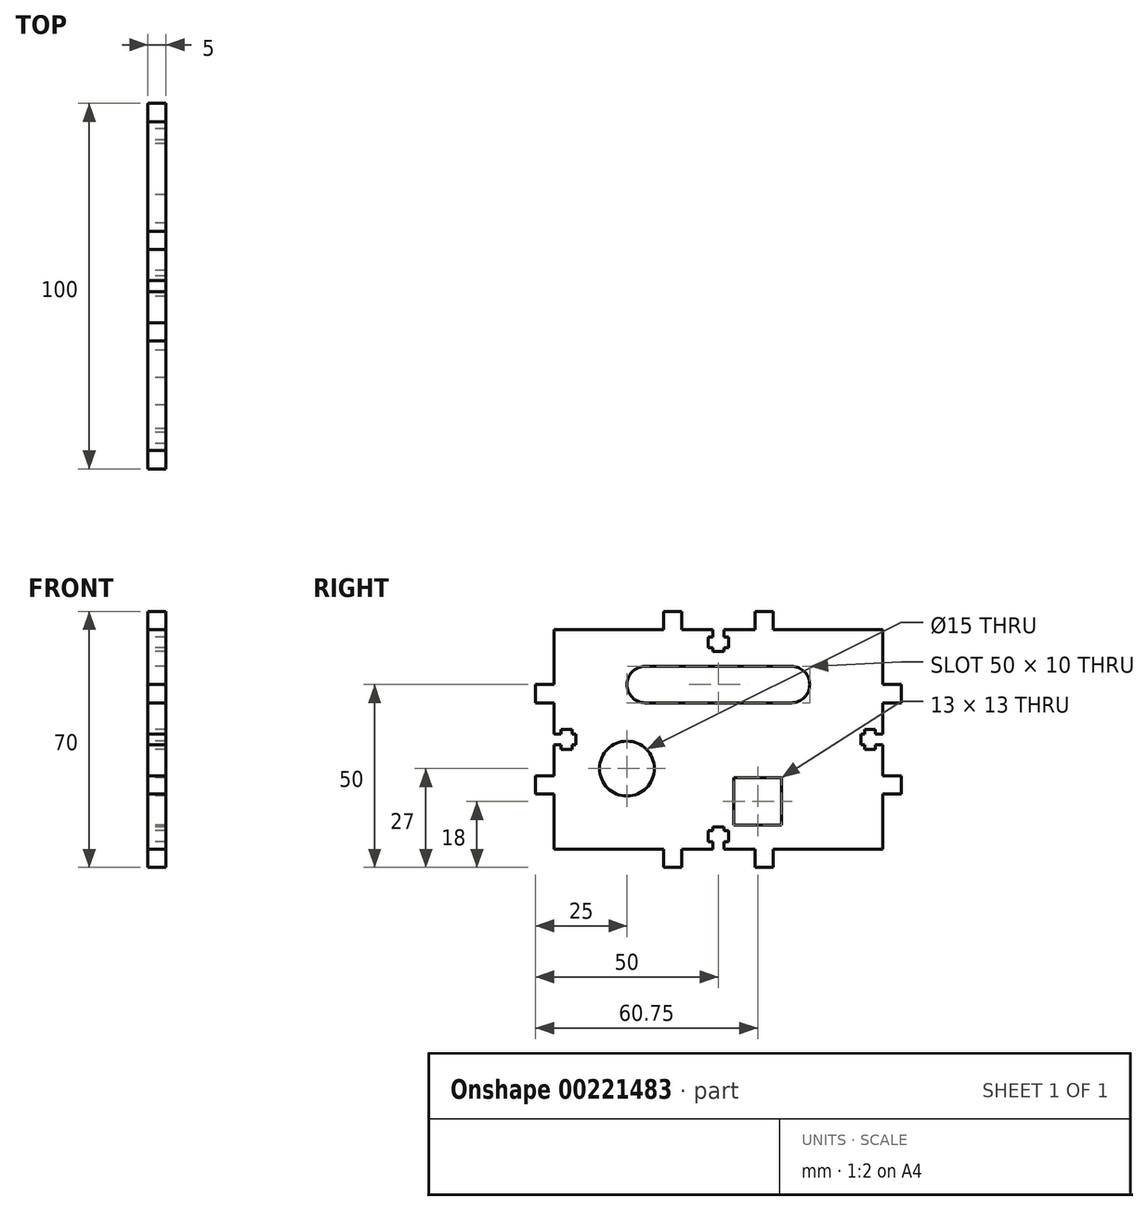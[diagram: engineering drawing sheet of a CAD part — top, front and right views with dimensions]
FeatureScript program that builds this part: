
annotation { "Feature Type Name" : "Feature", "Feature Type Description" : "" }
export const myFeature = defineFeature(function(context is Context, id is Id, definition is map)
    precondition{}
    {
        {
            assignVariable(context, id + "F0", {"name" : "thickness", "anyValue" : 5 * mm});
        }
        {
            var Q0;
            Q0=qCreatedBy(makeId("Right.planeOp"),FACE);
            var sketch = newSketch(context, id + "F1", { "sketchPlane" : qUnion([Q0])});
            skLineSegment(sketch, "E0.bottom", {"start": v(0, 0) * mm, "end": v(30, 0) * mm});
            skLineSegment(sketch, "E0.top", {"start": v(0, 60) * mm, "end": v(30, 60) * mm});
            skLineSegment(sketch, "E0.left", {"start": v(0, 0) * mm, "end": v(0, 15) * mm});
            skLineSegment(sketch, "E0.right", {"start": v(90, 0) * mm, "end": v(90, 15) * mm});
            skLineSegment(sketch, "E1", {"start": v(0, 45) * mm, "end": v(-5, 45) * mm});
            skLineSegment(sketch, "E2", {"start": v(-5, 45) * mm, "end": v(-5, 40) * mm});
            skLineSegment(sketch, "E3", {"start": v(-5, 40) * mm, "end": v(0, 40) * mm});
            skLineSegment(sketch, "E4", {"start": v(0, 20) * mm, "end": v(-5, 20) * mm});
            skLineSegment(sketch, "E5", {"start": v(-5, 20) * mm, "end": v(-5, 15) * mm});
            skLineSegment(sketch, "E6", {"start": v(-5, 15) * mm, "end": v(0, 15) * mm});
            skLineSegment(sketch, "E7", {"start": v(45, 60) * mm, "end": v(45, 0) * mm, "construction": true});
            skLineSegment(sketch, "E8", {"start": v(90, 30) * mm, "end": v(0, 30) * mm, "construction": true});
            skLineSegment(sketch, "E9", {"start": v(0, 31.5) * mm, "end": v(2, 31.5) * mm});
            skLineSegment(sketch, "E10", {"start": v(2, 31.5) * mm, "end": v(2, 32.75) * mm});
            skLineSegment(sketch, "E11", {"start": v(2, 32.75) * mm, "end": v(5, 32.75) * mm});
            skLineSegment(sketch, "E12", {"start": v(5, 32.75) * mm, "end": v(5, 31.5) * mm});
            skLineSegment(sketch, "E13", {"start": v(5, 27.25) * mm, "end": v(2, 27.25) * mm});
            skLineSegment(sketch, "E14", {"start": v(2, 27.25) * mm, "end": v(2, 28.5) * mm});
            skLineSegment(sketch, "E15", {"start": v(2, 28.5) * mm, "end": v(0, 28.5) * mm});
            skLineSegment(sketch, "E16", {"start": v(5, 31.5) * mm, "end": v(6, 31.5) * mm});
            skLineSegment(sketch, "E17", {"start": v(6, 31.5) * mm, "end": v(6, 28.5) * mm});
            skLineSegment(sketch, "E18", {"start": v(6, 28.5) * mm, "end": v(5, 28.5) * mm});
            skLineSegment(sketch, "E19.trimOffspring", {"start": v(5, 28.5) * mm, "end": v(5, 27.25) * mm});
            skPoint(sketch, "E20", {"position": v(6, 30) * mm});
            skLineSegment(sketch, "E21.MirrorCS", {"start": v(85, 31.5) * mm, "end": v(84, 31.5) * mm});
            skLineSegment(sketch, "E22.MirrorCS", {"start": v(88, 31.5) * mm, "end": v(88, 32.75) * mm});
            skLineSegment(sketch, "E23.MirrorCS", {"start": v(84, 28.5) * mm, "end": v(85, 28.5) * mm});
            skLineSegment(sketch, "E24.MirrorCS", {"start": v(88, 27.25) * mm, "end": v(88, 28.5) * mm});
            skLineSegment(sketch, "E25.MirrorCS", {"start": v(85, 32.75) * mm, "end": v(85, 31.5) * mm});
            skLineSegment(sketch, "E26.MirrorCS", {"start": v(85, 28.5) * mm, "end": v(85, 27.25) * mm});
            skLineSegment(sketch, "E27.MirrorCS", {"start": v(88, 28.5) * mm, "end": v(90, 28.5) * mm});
            skLineSegment(sketch, "E28.MirrorCS", {"start": v(84, 31.5) * mm, "end": v(84, 28.5) * mm});
            skLineSegment(sketch, "E29.MirrorCS", {"start": v(90, 31.5) * mm, "end": v(88, 31.5) * mm});
            skPoint(sketch, "E30.MirrorP", {"position": v(84, 30) * mm});
            skLineSegment(sketch, "E31.MirrorCS", {"start": v(85, 27.25) * mm, "end": v(88, 27.25) * mm});
            skLineSegment(sketch, "E32.MirrorCS", {"start": v(90, 45) * mm, "end": v(95, 45) * mm});
            skLineSegment(sketch, "E33.MirrorCS", {"start": v(95, 45) * mm, "end": v(95, 40) * mm});
            skLineSegment(sketch, "E34.MirrorCS", {"start": v(95, 40) * mm, "end": v(90, 40) * mm});
            skLineSegment(sketch, "E35.MirrorCS", {"start": v(88, 32.75) * mm, "end": v(85, 32.75) * mm});
            skLineSegment(sketch, "E36.MirrorCS", {"start": v(95, 15) * mm, "end": v(90, 15) * mm});
            skLineSegment(sketch, "E37.MirrorCS", {"start": v(90, 20) * mm, "end": v(95, 20) * mm});
            skLineSegment(sketch, "E38.MirrorCS", {"start": v(95, 20) * mm, "end": v(95, 15) * mm});
            skLineSegment(sketch, "E39", {"start": v(30, 0) * mm, "end": v(30, -5) * mm});
            skLineSegment(sketch, "E40", {"start": v(30, -5) * mm, "end": v(35, -5) * mm});
            skLineSegment(sketch, "E41", {"start": v(35, -5) * mm, "end": v(35, 0) * mm});
            skLineSegment(sketch, "E42", {"start": v(55, 0) * mm, "end": v(55, -5) * mm});
            skLineSegment(sketch, "E43", {"start": v(55, -5) * mm, "end": v(60, -5) * mm});
            skLineSegment(sketch, "E44", {"start": v(60, -5) * mm, "end": v(60, 0) * mm});
            skLineSegment(sketch, "E45", {"start": v(43.5, 0) * mm, "end": v(43.5, 2) * mm});
            skLineSegment(sketch, "E46", {"start": v(43.5, 2) * mm, "end": v(42.25, 2) * mm});
            skLineSegment(sketch, "E47", {"start": v(42.25, 2) * mm, "end": v(42.25, 5) * mm});
            skLineSegment(sketch, "E48", {"start": v(42.25, 5) * mm, "end": v(43.5, 5) * mm});
            skLineSegment(sketch, "E49", {"start": v(47.75, 5) * mm, "end": v(47.75, 2) * mm});
            skLineSegment(sketch, "E50", {"start": v(47.75, 2) * mm, "end": v(46.5, 2) * mm});
            skLineSegment(sketch, "E51", {"start": v(46.5, 2) * mm, "end": v(46.5, 0) * mm});
            skLineSegment(sketch, "E52", {"start": v(43.5, 5) * mm, "end": v(43.5, 6) * mm});
            skLineSegment(sketch, "E53", {"start": v(43.5, 6) * mm, "end": v(46.5, 6) * mm});
            skLineSegment(sketch, "E54", {"start": v(46.5, 6) * mm, "end": v(46.5, 5) * mm});
            skLineSegment(sketch, "E55.trimOffspring", {"start": v(46.5, 5) * mm, "end": v(47.75, 5) * mm});
            skPoint(sketch, "E56", {"position": v(45, 6) * mm});
            skLineSegment(sketch, "E57.MirrorCS", {"start": v(47.75, 58) * mm, "end": v(46.5, 58) * mm});
            skLineSegment(sketch, "E58.MirrorCS", {"start": v(43.5, 58) * mm, "end": v(42.25, 58) * mm});
            skLineSegment(sketch, "E59.MirrorCS", {"start": v(42.25, 55) * mm, "end": v(43.5, 55) * mm});
            skLineSegment(sketch, "E60.MirrorCS", {"start": v(43.5, 55) * mm, "end": v(43.5, 54) * mm});
            skLineSegment(sketch, "E61.MirrorCS", {"start": v(46.5, 55) * mm, "end": v(47.75, 55) * mm});
            skLineSegment(sketch, "E62.MirrorCS", {"start": v(46.5, 54) * mm, "end": v(46.5, 55) * mm});
            skLineSegment(sketch, "E63.MirrorCS", {"start": v(43.5, 54) * mm, "end": v(46.5, 54) * mm});
            skLineSegment(sketch, "E64.MirrorCS", {"start": v(43.5, 60) * mm, "end": v(43.5, 58) * mm});
            skLineSegment(sketch, "E65.MirrorCS", {"start": v(46.5, 58) * mm, "end": v(46.5, 60) * mm});
            skLineSegment(sketch, "E66.MirrorCS", {"start": v(35, 65) * mm, "end": v(35, 60) * mm});
            skPoint(sketch, "E67.MirrorP", {"position": v(45, 54) * mm});
            skLineSegment(sketch, "E68.MirrorCS", {"start": v(55, 60) * mm, "end": v(55, 65) * mm});
            skLineSegment(sketch, "E69.MirrorCS", {"start": v(47.75, 55) * mm, "end": v(47.75, 58) * mm});
            skLineSegment(sketch, "E70.MirrorCS", {"start": v(30, 65) * mm, "end": v(35, 65) * mm});
            skLineSegment(sketch, "E71.MirrorCS", {"start": v(30, 60) * mm, "end": v(30, 65) * mm});
            skLineSegment(sketch, "E72.MirrorCS", {"start": v(55, 65) * mm, "end": v(60, 65) * mm});
            skLineSegment(sketch, "E73.MirrorCS", {"start": v(42.25, 58) * mm, "end": v(42.25, 55) * mm});
            skLineSegment(sketch, "E74.MirrorCS", {"start": v(60, 65) * mm, "end": v(60, 60) * mm});
            skLineSegment(sketch, "E75.trimOffspring", {"start": v(0, 31.5) * mm, "end": v(0, 40) * mm});
            skLineSegment(sketch, "E76.trimOffspring", {"start": v(0, 45) * mm, "end": v(0, 60) * mm});
            skLineSegment(sketch, "E77.trimOffspring", {"start": v(0, 20) * mm, "end": v(0, 28.5) * mm});
            skLineSegment(sketch, "E78.trimOffspring", {"start": v(35, 0) * mm, "end": v(43.5, 0) * mm});
            skLineSegment(sketch, "E79.trimOffspring", {"start": v(46.5, 0) * mm, "end": v(55, 0) * mm});
            skLineSegment(sketch, "E80.trimOffspring", {"start": v(60, 0) * mm, "end": v(90, 0) * mm});
            skLineSegment(sketch, "E81.trimOffspring", {"start": v(90, 20) * mm, "end": v(90, 28.5) * mm});
            skLineSegment(sketch, "E82.trimOffspring", {"start": v(90, 31.5) * mm, "end": v(90, 40) * mm});
            skLineSegment(sketch, "E83.trimOffspring", {"start": v(90, 45) * mm, "end": v(90, 60) * mm});
            skLineSegment(sketch, "E84.trimOffspring", {"start": v(60, 60) * mm, "end": v(90, 60) * mm});
            skLineSegment(sketch, "E85.trimOffspring", {"start": v(35, 60) * mm, "end": v(43.5, 60) * mm});
            skLineSegment(sketch, "E86.trimOffspring", {"start": v(46.5, 60) * mm, "end": v(55, 60) * mm});
            skLineSegment(sketch, "E87", {"start": v(65, 45) * mm, "end": v(25, 45) * mm});
            skPoint(sketch, "E88", {"position": v(45, 45) * mm});
            skArc(sketch, "E89.0.startCap", {"start": v(65, 50) * mm, "mid": v(70, 45) * mm, "end": v(65, 40) * mm});
            skArc(sketch, "E89.0.endCap", {"start": v(25, 40) * mm, "mid": v(20, 45) * mm, "end": v(25, 50) * mm});
            skLineSegment(sketch, "E89.0.left", {"start": v(65, 40) * mm, "end": v(25, 40) * mm});
            skLineSegment(sketch, "E89.0.right", {"start": v(65, 50) * mm, "end": v(25, 50) * mm});
            skCircle(sketch, "E90", {"center": v(20, 22) * mm, "radius": 7.5 * mm});
            skLineSegment(sketch, "E91.bottom", {"start": v(49.25, 19.5) * mm, "end": v(62.25, 19.5) * mm});
            skLineSegment(sketch, "E91.top", {"start": v(49.25, 6.5) * mm, "end": v(62.25, 6.5) * mm});
            skLineSegment(sketch, "E91.left", {"start": v(49.25, 19.5) * mm, "end": v(49.25, 6.5) * mm});
            skLineSegment(sketch, "E91.right", {"start": v(62.25, 19.5) * mm, "end": v(62.25, 6.5) * mm});
            skSolve(sketch);
        }
        {
            var Q0;
            Q0=makeQuery(id+"F1.imprint","IMPRINT",FACE,{"disambiguationData":[TD([[makeQuery(id+"F1.imprint","IMPRINT",EDGE,{"derivedFrom":sQuery(id+"F1.wireOp",EDGE,"E0.bottom")}),1.0]])]});
            extrude(context, id + "F2", {"entities" : qUnion([Q0]), "depth" : getVariable(context, 'thickness')});
        }
    });
